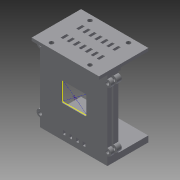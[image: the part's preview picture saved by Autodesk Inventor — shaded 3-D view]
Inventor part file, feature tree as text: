
AUTODESK INVENTOR PART (.ipt)
format: ipt  version: 2013 (Build 170138000, 138)  size: 496,640 bytes
history: native  units: in
note: dims shown in document units (in); Inventor stores cm internally (conversion verified against a paired STEP export)
features: sketch x18, extrude x17, reference x9, projected_geometry x1
ambient origin geometry x8: Origin, YZ Plane, XZ Plane, XY Plane, X Axis, Y Axis, Z Axis, Center Point
bodies: Solid1 (feature_tree)
feature tree (45):
  extrude  "Extrusion1"  Depth=0.1181in
  extrude  "Extrusion14"  Depth=0.1181in
  extrude  "Extrusion17"  Depth=0.3543in TaperAngle=0.0deg
  extrude  "Extrusion26"  Depth=0.2756in
  extrude  "Extrusion27"  Depth=0.1181in
  extrude  "Extrusion32"  Depth=0.0787in TaperAngle=0.0deg
  extrude  "Extrusion34"  Depth=0.8189in
  extrude  "Extrusion36"  Depth=0.0787in TaperAngle=0.0deg
  extrude  "Extrusion37"  Depth=0.0787in
  sketch  "Sketch39"  dims[d115=0.0394in d140=0.0787in]
  extrude  "Extrusion38"  Depth=0.1181in TaperAngle=0.0deg
  extrude  "Extrusion41"  Depth=0.1575in
  extrude  "Extrusion42"  Depth=0.1969in
  extrude  "Extrusion44"  Depth=0.0591in TaperAngle=0.0deg
  extrude  "Extrusion45"  Depth=0.3937in
  extrude  "Extrusion46"  Depth=0.3937in TaperAngle=0.0deg
  extrude  "Extrusion47"  Depth=0.1181in TaperAngle=0.0deg
  extrude  "Extrusion48"  Depth=1.3476in
  sketch  "Sketch1"  dims[d0=2.2in d2=0.1181in]
  reference  "Reference1"
  sketch  "Sketch14"  dims[d3=0.2362in d4=0.1181in d5=0.2362in d6=1.95in]
  reference  "Reference2"
  reference  "Reference3"
  reference  "Reference4"
  reference  "Reference5"
  sketch  "Sketch17"  dims[d8=0.1181in d9=0.3543in d10=0.0in]
  sketch  "Sketch26"  dims[d11=0.1181in d12=0.1181in d14=0.0787in d16=0.2756in]
  reference  "Reference6"
  reference  "Reference7"
  sketch  "Sketch27"  dims[d17=0.2756in]
  reference  "Reference8"
  reference  "Reference9"
  sketch  "Sketch32"  dims[d35=0.3937in d36=0.5906in d37=0.7874in d38=0.9843in d39=0.3937in d40=0.5906in d41=1.1811in d42=1.378in d43=1.5748in d44=1.7717in d78=0.1181in]
  sketch  "Sketch35"  dims[d79=0.1181in d94=0.0787in d95=0.0in]
  sketch  "Sketch37"  dims[d96=1.811in d111=0.8189in]
  sketch  "Sketch38"  dims[d112=0.6339in d113=0.0787in d114=0.0in]
  sketch  "Sketch40"  dims[d141=0.1575in d142=0.1181in d143=0.0787in d144=0.0in d145=0.0in]
  sketch  "Sketch43"  dims[d146=0.0787in d147=0.1575in]
  sketch  "Sketch44"  dims[d148=0.0591in d149=0.1181in d150=0.0in d151=0.0in d180=0.1969in]
  projected_geometry  "Projected Loop5"
  sketch  "Sketch46"  dims[d182=0.9843in d183=0.0in d184=0.0591in d185=0.0in]
  sketch  "Sketch48"  dims[d194=0.25in d195=0.3937in]
  sketch  "Sketch49"  dims[d196=0.25in d197=0.0787in d198=0.3937in d199=0.0in]
  sketch  "Sketch50"  dims[d206=2.2in d207=0.1181in d208=0.0in]
  sketch  "Sketch51"  dims[d209=1.3476in d211=1.3476in d212=0.0394in d213=0.0in d214=0.1772in d215=0.1181in d216=0.0984in d217=2.2in d218=0.2756in d219=1.3386in d220=0.0in d221=0.0in d233=0.0394in d234=0.0394in d235=0.0787in d236=0.3543in d237=2.7559in d239=0.1969in d240=0.3937in d242=0.3937in d245=0.1969in d246=0.0in d247=0.0394in d248=0.0394in d249=0.0787in d250=0.0787in d251=3.5433in d253=0.2165in d254=0.3937in d256=0.3937in d258=0.1969in d259=0.0in d260=0.074in d275=0.1339in d277=0.1339in d278=1.2598in d279=1.2598in d280=0.1969in d281=0.0in d282=0.1575in d284=1.8898in d285=0.0394in d286=0.0787in d287=0.0in d288=0.0787in d289=0.0in d291=0.3937in d292=0.0in d294=0.1339in d295=0.1181in d296=0.1181in d297=0.3496in d298=0.1969in d299=0.8268in d300=0.0in d301=0.0787in d302=0.1181in d303=0.5906in d304=0.3937in d305=0.0in d306=1.5748in d308=0.2165in d309=0.3937in d311=0.3937in]
